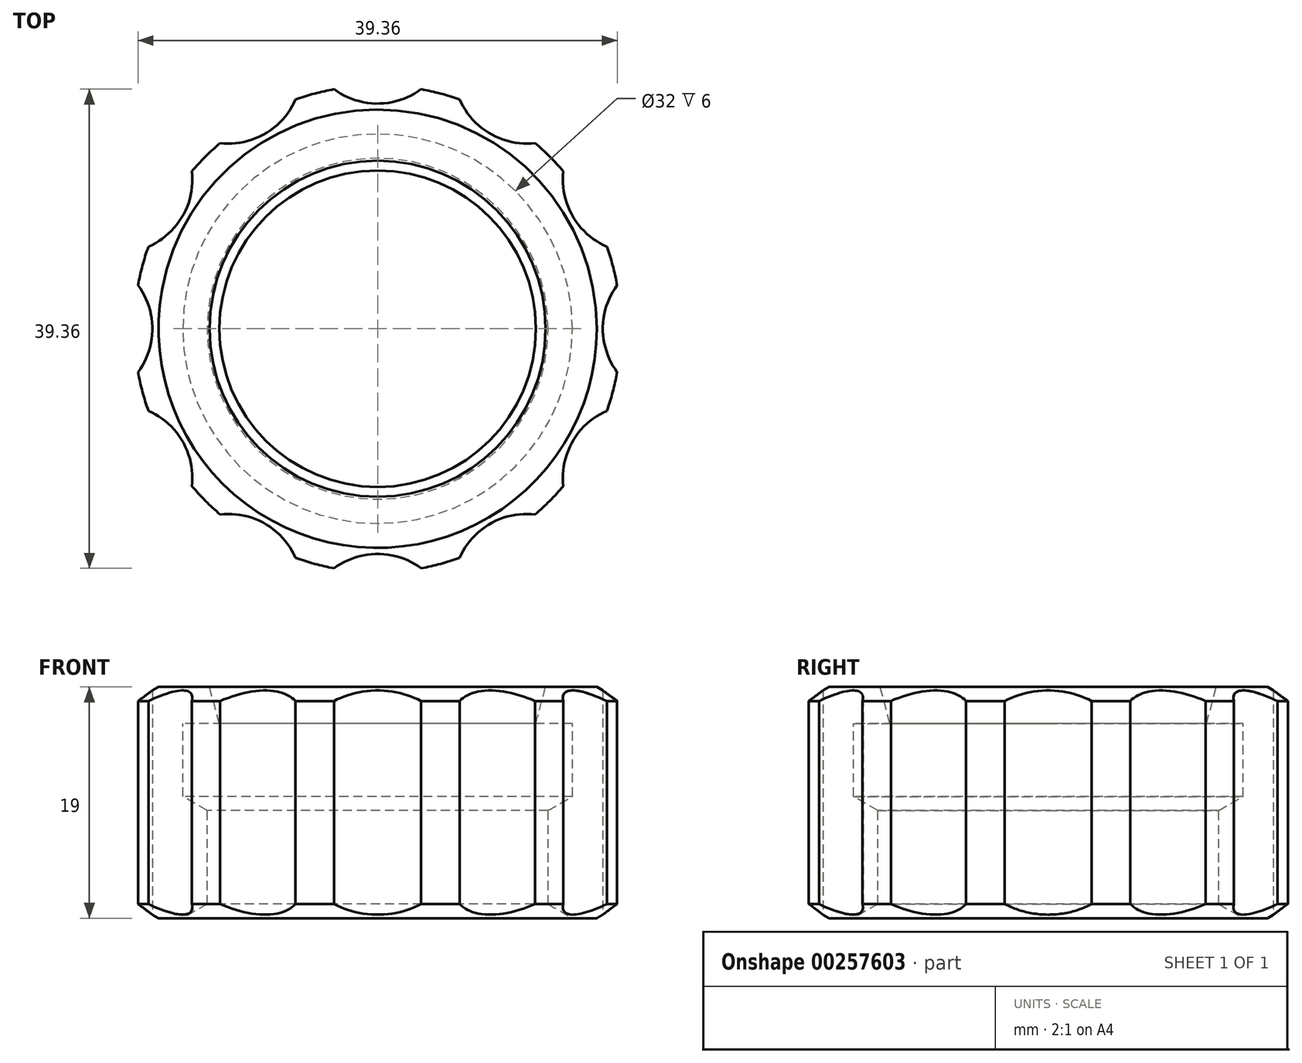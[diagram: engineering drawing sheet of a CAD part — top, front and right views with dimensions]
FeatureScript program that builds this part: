
annotation { "Feature Type Name" : "Feature", "Feature Type Description" : "" }
export const myFeature = defineFeature(function(context is Context, id is Id, definition is map)
    precondition{}
    {
        {
            var Q0;
            Q0=qCreatedBy(makeId("Front.planeOp"),FACE);
            var sketch = newSketch(context, id + "F0", { "sketchPlane" : qUnion([Q0])});
            skLineSegment(sketch, "E0", {"start": v(-13, 16) * mm, "end": v(-16, 16) * mm});
            skLineSegment(sketch, "E1", {"start": v(-16, 16) * mm, "end": v(-16, 10) * mm});
            skLineSegment(sketch, "E2", {"start": v(-16, 10) * mm, "end": v(-14, 8.85) * mm});
            skLineSegment(sketch, "E3", {"start": v(-14, 8.85) * mm, "end": v(-14, 1.15) * mm});
            skLineSegment(sketch, "E4", {"start": v(-14, 1.15) * mm, "end": v(-16, 0) * mm});
            skLineSegment(sketch, "E5", {"start": v(-16, 0) * mm, "end": v(-18, 0) * mm});
            skLineSegment(sketch, "E6", {"start": v(-18, 0) * mm, "end": v(-20, 1.15) * mm});
            skLineSegment(sketch, "E7", {"start": v(-20, 1.15) * mm, "end": v(-20, 17.85) * mm});
            skLineSegment(sketch, "E8", {"start": v(-20, 17.85) * mm, "end": v(-18, 19) * mm});
            skLineSegment(sketch, "E9", {"start": v(-18, 19) * mm, "end": v(-13.8, 19) * mm});
            skLineSegment(sketch, "E10", {"start": v(-13.8, 19) * mm, "end": v(-13, 16) * mm});
            skLineSegment(sketch, "E11", {"start": v(0, 19) * mm, "end": v(0, 0) * mm, "construction": true});
            skSolve(sketch);
        }
        {
            var Q0;
            Q0 = qSketchRegion(id + "F0", true);
            var Q1;
            Q1=sQuery(id+"F0.wireOp",EDGE,"E11");
            revolve(context, id + "F1", {"entities" : qUnion([Q0]), "axis" : qUnion([Q1]), "revolveType" : RevolveType.FULL});
        }
        {
            var Q0;
            Q0=makeQuery(id+"F1.opRevolve","SWEPT_FACE",FACE,{"disambiguationData":[OSD([sQuery(id+"F0.wireOp",EDGE,"E5")])]});
            var sketch = newSketch(context, id + "F2", { "sketchPlane" : qUnion([Q0])});
            skCircle(sketch, "E12", {"center": v(24.5, 0) * mm, "radius": 6 * mm});
            skCircle(sketch, "E13.1.0", {"center": v(21.22, 12.25) * mm, "radius": 6 * mm});
            skCircle(sketch, "E13.2.0", {"center": v(12.25, 21.22) * mm, "radius": 6 * mm});
            skCircle(sketch, "E13.3.0", {"center": v(0, 24.5) * mm, "radius": 6 * mm});
            skCircle(sketch, "E13.4.0", {"center": v(-12.25, 21.22) * mm, "radius": 6 * mm});
            skCircle(sketch, "E13.5.0", {"center": v(-21.22, 12.25) * mm, "radius": 6 * mm});
            skCircle(sketch, "E13.6.0", {"center": v(-24.5, 0) * mm, "radius": 6 * mm});
            skCircle(sketch, "E13.7.0", {"center": v(-21.22, -12.25) * mm, "radius": 6 * mm});
            skCircle(sketch, "E13.8.0", {"center": v(-12.25, -21.22) * mm, "radius": 6 * mm});
            skCircle(sketch, "E13.9.0", {"center": v(0, -24.5) * mm, "radius": 6 * mm});
            skCircle(sketch, "E13.10.0", {"center": v(12.25, -21.22) * mm, "radius": 6 * mm});
            skCircle(sketch, "E13.11.0", {"center": v(21.22, -12.25) * mm, "radius": 6 * mm});
            skPoint(sketch, "E13.center", {"position": v(0, 0) * mm});
            skSolve(sketch);
        }
        {
            var Q0;
            Q0 = qSketchRegion(id + "F2", true);
            extrude(context, id + "F3", {"entities" : qUnion([Q0]), "operationType" : NewBodyOperationType.REMOVE, "endBound" : BoundingType.THROUGH_ALL, "oppositeDirection" : true, "depth" : 25 * mm});
        }
    });
